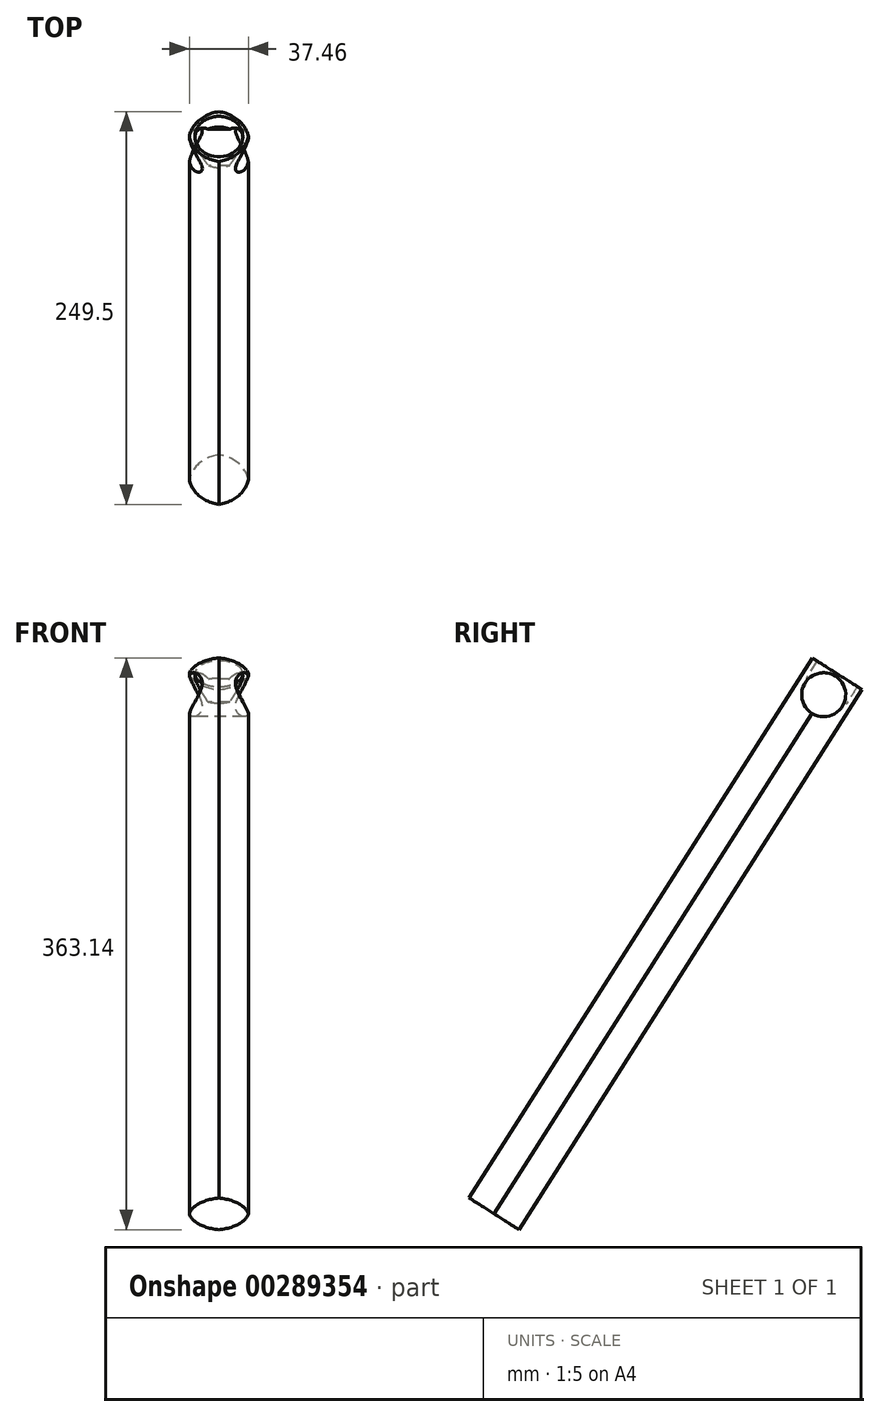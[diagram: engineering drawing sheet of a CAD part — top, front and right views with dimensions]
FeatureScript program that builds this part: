
annotation { "Feature Type Name" : "Feature", "Feature Type Description" : "" }
export const myFeature = defineFeature(function(context is Context, id is Id, definition is map)
    precondition{}
    {
        {
            var Q0;
            Q0=qCreatedBy(makeId("Right.planeOp"),FACE);
            var sketch = newSketch(context, id + "F0", { "sketchPlane" : qUnion([Q0])});
            skLineSegment(sketch, "E0", {"start": v(111.05, 355.6) * mm, "end": v(111.05, 12.55) * mm, "construction": true});
            skLineSegment(sketch, "E1", {"start": v(111.05, 355.6) * mm, "end": v(-106.83, 12.55) * mm});
            skLineSegment(sketch, "E2", {"start": v(-106.83, 12.55) * mm, "end": v(-74.67, -7.88) * mm});
            skLineSegment(sketch, "E3", {"start": v(-74.67, -7.88) * mm, "end": v(143.21, 335.17) * mm});
            skLineSegment(sketch, "E4", {"start": v(143.21, 335.17) * mm, "end": v(111.05, 355.6) * mm});
            skLineSegment(sketch, "E5", {"start": v(0, 177.8) * mm, "end": v(111.05, 177.8) * mm, "construction": true});
            skLineSegment(sketch, "E6", {"start": v(111.05, 177.8) * mm, "end": v(311.42, 177.8) * mm, "construction": true});
            skLineSegment(sketch, "E7", {"start": v(311.42, 177.8) * mm, "end": v(-196.86, 177.8) * mm, "construction": true});
            skLineSegment(sketch, "E8", {"start": v(0, 355.6) * mm, "end": v(339.66, 355.6) * mm, "construction": true});
            skLineSegment(sketch, "E9", {"start": v(339.66, 355.6) * mm, "end": v(-216.18, 355.6) * mm, "construction": true});
            skLineSegment(sketch, "E10", {"start": v(0, 355.6) * mm, "end": v(0, -7.88) * mm, "construction": true});
            skLineSegment(sketch, "E11", {"start": v(0, -7.88) * mm, "end": v(-74.67, -7.88) * mm, "construction": true});
            skPoint(sketch, "E12", {"position": v(-79.46, 19.04) * mm});
            skLineSegment(sketch, "E13", {"start": v(127.13, 345.39) * mm, "end": v(100.16, 303.45) * mm, "construction": true});
            skLineSegment(sketch, "E14", {"start": v(93.91, 328.61) * mm, "end": v(126.07, 308.19) * mm, "construction": true});
            skLineSegment(sketch, "E15", {"start": v(126.07, 308.19) * mm, "end": v(111.05, 317.73) * mm, "construction": true});
            skCircle(sketch, "E16", {"center": v(118.58, 332.08) * mm, "radius": 13.97 * mm});
            skSolve(sketch);
        }
        {
            var Q0;
            Q0=makeQuery(id+"F0.imprint","IMPRINT",FACE,{"disambiguationData":[TD([[makeQuery(id+"F0.imprint","IMPRINT",EDGE,{"derivedFrom":sQuery(id+"F0.wireOp",EDGE,"E1")}),1.0]])]});
            extrude(context, id + "F1", {"entities" : qUnion([Q0]), "endBound" : BoundingType.SYMMETRIC, "depth" : 38.1 * mm});
        }
        {
            var Q0;
            Q0=makeQuery(id+"F1.opExtrude","CAP_EDGE",EDGE,{"disambiguationData":[OSD([sQuery(id+"F0.wireOp",EDGE,"E1")])],"isStart":false});
            var Q1;
            Q1=makeQuery(id+"F1.opExtrude","CAP_EDGE",EDGE,{"disambiguationData":[OSD([sQuery(id+"F0.wireOp",EDGE,"E1")])],"isStart":true});
            var Q2;
            Q2=makeQuery(id+"F1.opExtrude","CAP_EDGE",EDGE,{"disambiguationData":[OSD([sQuery(id+"F0.wireOp",EDGE,"E3")])],"isStart":false});
            var Q3;
            Q3=makeQuery(id+"F1.opExtrude","CAP_EDGE",EDGE,{"disambiguationData":[OSD([sQuery(id+"F0.wireOp",EDGE,"E3")])],"isStart":true});
            fillet(context, id + "F2", {"entities" : qUnion([Q0, Q1, Q2, Q3]), "radius" : 22.86 * mm, "tangentPropagation" : true, "allowEdgeOverflow" : false});
        }
        {
            var Q0;
            Q0=makeQuery(id+"F1.opExtrude","SWEPT_FACE",FACE,{"disambiguationData":[OSD([sQuery(id+"F0.wireOp",EDGE,"E4")])]});
            var sketch = newSketch(context, id + "F3", { "sketchPlane" : qUnion([Q0])});
            skLineSegment(sketch, "E17", {"start": v(0, -96.59) * mm, "end": v(0, -59.13) * mm, "construction": true});
            skLineSegment(sketch, "E18", {"start": v(0, -59.13) * mm, "end": v(0, -77.86) * mm, "construction": true});
            skLineSegment(sketch, "E19", {"start": v(0, -77.86) * mm, "end": v(-18.73, -77.86) * mm, "construction": true});
            skLineSegment(sketch, "E20", {"start": v(-18.73, -77.86) * mm, "end": v(18.73, -77.86) * mm, "construction": true});
            skCircle(sketch, "E21", {"center": v(0, -77.86) * mm, "radius": 15.24 * mm});
            skSolve(sketch);
        }
        {
            var Q0;
            Q0=makeQuery(id+"F3.imprint","IMPRINT",FACE,{"disambiguationData":[TD([[makeQuery(id+"F3.imprint","IMPRINT",EDGE,{"derivedFrom":sQuery(id+"F3.wireOp",EDGE,"E21")}),1.0]])]});
            extrude(context, id + "F4", {"entities" : qUnion([Q0]), "operationType" : NewBodyOperationType.REMOVE, "endBound" : BoundingType.SYMMETRIC, "depth" : 25.4 * mm});
        }
    });
